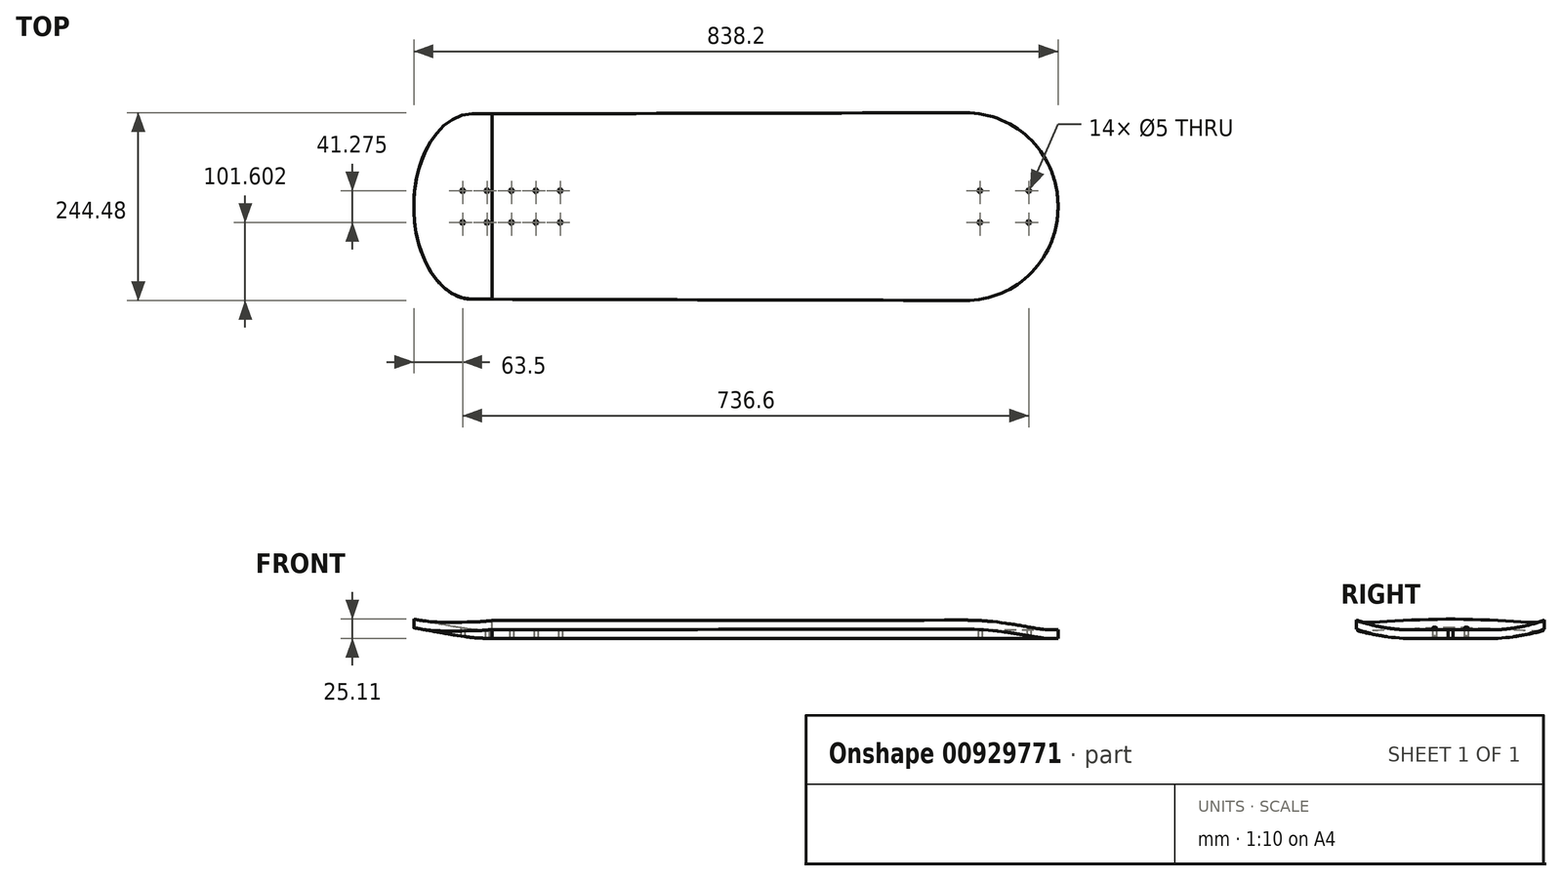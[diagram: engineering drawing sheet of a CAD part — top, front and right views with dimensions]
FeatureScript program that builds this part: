
annotation { "Feature Type Name" : "Feature", "Feature Type Description" : "" }
export const myFeature = defineFeature(function(context is Context, id is Id, definition is map)
    precondition{}
    {
        {
            var Q0;
            Q0=qCreatedBy(makeId("Front.planeOp"),FACE);
            var sketch = newSketch(context, id + "F0", { "sketchPlane" : qUnion([Q0])});
            skPoint(sketch, "E0", {"position": v(-774.7, 0) * mm});
            skPoint(sketch, "E1", {"position": v(-711.2, 0) * mm});
            skPoint(sketch, "E2", {"position": v(-742.95, 0) * mm});
            skPoint(sketch, "E3", {"position": v(-38.1, 0) * mm});
            skPoint(sketch, "E4", {"position": v(-647.7, 0) * mm});
            skPoint(sketch, "E5", {"position": v(-679.45, 0) * mm});
            skPoint(sketch, "E6", {"position": v(-101.6, 0) * mm});
            skLineSegment(sketch, "E7", {"start": v(0, 0) * mm, "end": v(-736.6, 0) * mm});
            skLineSegment(sketch, "E8", {"start": v(-780.7, 3.86) * mm, "end": v(-838.2, 14) * mm});
            skArc(sketch, "E9.filletArc", {"start": v(-780.7, 3.86) * mm, "mid": v(-758.74, 0.97) * mm, "end": v(-736.6, 0) * mm});
            skSolve(sketch);
        }
        {
            var Q0;
            Q0=qCreatedBy(makeId("Top.planeOp"),FACE);
            var sketch = newSketch(context, id + "F1", { "sketchPlane" : qUnion([Q0])});
            skLineSegment(sketch, "E10", {"start": v(-762.12, 120.65) * mm, "end": v(-120.94, 122.24) * mm});
            skLineSegment(sketch, "E11", {"start": v(-120.94, -122.24) * mm, "end": v(-762.12, -120.65) * mm});
            skArc(sketch, "E12.filletArc", {"start": v(0, 0) * mm, "mid": v(-34.87, 86.44) * mm, "end": v(-120.94, 122.24) * mm});
            skArc(sketch, "E13.filletArc", {"start": v(-120.94, -122.24) * mm, "mid": v(-34.87, -86.44) * mm, "end": v(0, 0) * mm});
            skPoint(sketch, "E14.visualSharp", {"position": v(-762.12, 120.65) * mm});
            skPoint(sketch, "E15.visualSharp", {"position": v(-762.12, -120.65) * mm});
            skPoint(sketch, "E16", {"position": v(-120.64, -122.24) * mm});
            skPoint(sketch, "E17", {"position": v(-120.64, 122.24) * mm});
            skPoint(sketch, "E18.5", {"position": v(-774.7, 0) * mm});
            skPoint(sketch, "E18.6", {"position": v(-711.2, 0) * mm});
            skPoint(sketch, "E18.7", {"position": v(-742.95, 0) * mm});
            skPoint(sketch, "E18.8", {"position": v(-38.1, 0) * mm});
            skPoint(sketch, "E18.9", {"position": v(-647.7, 0) * mm});
            skPoint(sketch, "E18.10", {"position": v(-679.45, 0) * mm});
            skPoint(sketch, "E18.11", {"position": v(-101.6, 0) * mm});
            skLineSegment(sketch, "E19", {"start": v(-774.7, 0) * mm, "end": v(-774.7, 20.64) * mm, "construction": true});
            skLineSegment(sketch, "E20", {"start": v(-711.2, 20.64) * mm, "end": v(-711.2, 0) * mm, "construction": true});
            skLineSegment(sketch, "E21", {"start": v(-38.1, 0) * mm, "end": v(-38.1, 20.64) * mm, "construction": true});
            skLineSegment(sketch, "E22", {"start": v(-647.7, 0) * mm, "end": v(-647.7, 20.64) * mm, "construction": true});
            skLineSegment(sketch, "E23", {"start": v(-101.6, 0) * mm, "end": v(-101.6, 20.64) * mm, "construction": true});
            skLineSegment(sketch, "E24", {"start": v(-679.45, 0) * mm, "end": v(-679.45, 20.64) * mm, "construction": true});
            skLineSegment(sketch, "E25", {"start": v(-742.95, 0) * mm, "end": v(-742.95, 20.64) * mm, "construction": true});
            skCircle(sketch, "E26", {"center": v(-774.7, 20.64) * mm, "radius": 2.5 * mm});
            skCircle(sketch, "E27", {"center": v(-711.2, 20.64) * mm, "radius": 2.5 * mm});
            skCircle(sketch, "E28", {"center": v(-742.95, 20.64) * mm, "radius": 2.5 * mm});
            skCircle(sketch, "E29", {"center": v(-679.45, 20.64) * mm, "radius": 2.5 * mm});
            skCircle(sketch, "E30", {"center": v(-101.6, 20.64) * mm, "radius": 2.5 * mm});
            skCircle(sketch, "E31", {"center": v(-647.7, 20.64) * mm, "radius": 2.5 * mm});
            skCircle(sketch, "E32", {"center": v(-38.1, 20.64) * mm, "radius": 2.5 * mm});
            skCircle(sketch, "E33.MirrorC", {"center": v(-38.1, -20.64) * mm, "radius": 2.5 * mm});
            skCircle(sketch, "E34.MirrorC", {"center": v(-647.7, -20.64) * mm, "radius": 2.5 * mm});
            skCircle(sketch, "E35.MirrorC", {"center": v(-101.6, -20.64) * mm, "radius": 2.5 * mm});
            skCircle(sketch, "E36.MirrorC", {"center": v(-679.45, -20.64) * mm, "radius": 2.5 * mm});
            skCircle(sketch, "E37.MirrorC", {"center": v(-742.95, -20.64) * mm, "radius": 2.5 * mm});
            skCircle(sketch, "E38.MirrorC", {"center": v(-711.2, -20.64) * mm, "radius": 2.5 * mm});
            skCircle(sketch, "E39.MirrorC", {"center": v(-774.7, -20.64) * mm, "radius": 2.5 * mm});
            skLineSegment(sketch, "E40", {"start": v(-647.7, 0) * mm, "end": v(-647.7, -20.64) * mm, "construction": true});
            skPoint(sketch, "E41", {"position": v(-838.2, 0) * mm});
            skEllipticalArc(sketch, "E42", {});
            skPoint(sketch, "E43", {"position": v(-762, -120.65) * mm});
            const initialGuessF1  = {"E42": [-0.762, 0, 0, 1, 0.12065014743999705, 0.0762, 0.001563359187813156, 3.141592653589793]};
            skSetInitialGuess(sketch, initialGuessF1);
            skSolve(sketch);
        }
        {
            var Q0;
            Q0=sQuery(id+"F0.wireOp",VERTEX,"E8.end");
            var Q1;
            Q1=sQuery(id+"F0.wireOp",EDGE,"E8");
            cPlane(context, id + "F2", {"entities" : qUnion([Q0, Q1]), "cplaneType" : CPlaneType.LINE_POINT, "offset" : 25.4 * mm, "width" : 152.4 * mm, "height" : 152.4 * mm});
        }
        {
            var Q0;
            Q0=sQuery(id+"F0.wireOp",VERTEX,"E7.end");
            var Q1;
            Q1=sQuery(id+"F0.wireOp",EDGE,"E7");
            cPlane(context, id + "F3", {"entities" : qUnion([Q0, Q1]), "cplaneType" : CPlaneType.LINE_POINT, "offset" : 25.4 * mm, "width" : 152.4 * mm, "height" : 152.4 * mm});
        }
        {
            var Q0;
            Q0=sQuery(id+"F0.wireOp",VERTEX,"E7.start");
            var Q1;
            Q1=sQuery(id+"F0.wireOp",EDGE,"E7");
            cPlane(context, id + "F4", {"entities" : qUnion([Q0, Q1]), "cplaneType" : CPlaneType.LINE_POINT, "offset" : 25.4 * mm, "width" : 152.4 * mm, "height" : 152.4 * mm});
        }
        {
            var Q0;
            Q0=qCreatedBy(id+"F4.planeOp",FACE);
            var sketch = newSketch(context, id + "F5", { "sketchPlane" : qUnion([Q0])});
            skLineSegment(sketch, "E44", {"start": v(0, -32.26) * mm, "end": v(0, 0) * mm, "construction": true});
            skLineSegment(sketch, "E45", {"start": v(0, 218.6) * mm, "end": v(0, 0) * mm, "construction": true});
            skLineSegment(sketch, "E46", {"start": v(0, 0) * mm, "end": v(-50.8, 0) * mm});
            skArc(sketch, "E47", {"start": v(-122.24, 12.7) * mm, "mid": v(-87.08, 3.2) * mm, "end": v(-50.8, 0) * mm});
            skArc(sketch, "E48", {"start": v(-122.24, 0.9) * mm, "mid": v(-87.02, -8.09) * mm, "end": v(-50.8, -11.11) * mm});
            skLineSegment(sketch, "E49", {"start": v(-122.24, 12.7) * mm, "end": v(-122.24, 0.9) * mm});
            skLineSegment(sketch, "E50", {"start": v(-50.8, -11.11) * mm, "end": v(0, -11.11) * mm});
            skLineSegment(sketch, "E51.MirrorCS", {"start": v(122.24, 12.7) * mm, "end": v(122.24, 0.9) * mm});
            skArc(sketch, "E52.MirrorCS", {"start": v(122.24, 0.9) * mm, "mid": v(87.02, -8.09) * mm, "end": v(50.8, -11.11) * mm});
            skLineSegment(sketch, "E53.MirrorCS", {"start": v(0, 0) * mm, "end": v(50.8, 0) * mm});
            skLineSegment(sketch, "E54.MirrorCS", {"start": v(50.8, -11.11) * mm, "end": v(0, -11.11) * mm});
            skArc(sketch, "E55.MirrorCS", {"start": v(122.24, 12.7) * mm, "mid": v(87.08, 3.2) * mm, "end": v(50.8, 0) * mm});
            skSolve(sketch);
        }
        {
            var Q0;
            Q0=qCreatedBy(id+"F3.planeOp",FACE);
            var sketch = newSketch(context, id + "F6", { "sketchPlane" : qUnion([Q0])});
            skLineSegment(sketch, "E56.0", {"start": v(0, -32.26) * mm, "end": v(0, 0) * mm, "construction": true});
            skLineSegment(sketch, "E56.1", {"start": v(0, 218.6) * mm, "end": v(0, 0) * mm, "construction": true});
            skLineSegment(sketch, "E56.2", {"start": v(0, 0) * mm, "end": v(-50.8, 0) * mm});
            skArc(sketch, "E56.3", {"start": v(-122.24, 12.7) * mm, "mid": v(-87.08, 3.2) * mm, "end": v(-50.8, 0) * mm});
            skArc(sketch, "E56.4", {"start": v(-122.24, 0.9) * mm, "mid": v(-87.02, -8.09) * mm, "end": v(-50.8, -11.11) * mm});
            skLineSegment(sketch, "E56.5", {"start": v(-122.24, 12.7) * mm, "end": v(-122.24, 0.9) * mm});
            skLineSegment(sketch, "E56.6", {"start": v(-50.8, -11.11) * mm, "end": v(0, -11.11) * mm});
            skLineSegment(sketch, "E56.7", {"start": v(122.24, 12.7) * mm, "end": v(122.24, 0.9) * mm});
            skArc(sketch, "E56.8", {"start": v(122.24, 0.9) * mm, "mid": v(87.02, -8.09) * mm, "end": v(50.8, -11.11) * mm});
            skLineSegment(sketch, "E56.9", {"start": v(0, 0) * mm, "end": v(50.8, 0) * mm});
            skLineSegment(sketch, "E56.10", {"start": v(50.8, -11.11) * mm, "end": v(0, -11.11) * mm});
            skArc(sketch, "E56.11", {"start": v(122.24, 12.7) * mm, "mid": v(87.08, 3.2) * mm, "end": v(50.8, 0) * mm});
            skSolve(sketch);
        }
        {
            var Q0;
            Q0=qCreatedBy(id+"F2.planeOp",FACE);
            var sketch = newSketch(context, id + "F7", { "sketchPlane" : qUnion([Q0])});
            skLineSegment(sketch, "E57", {"start": v(0, -131.77) * mm, "end": v(-50.8, -131.77) * mm});
            skLineSegment(sketch, "E58", {"start": v(-50.8, -131.77) * mm, "end": v(-122.24, -131.77) * mm});
            skLineSegment(sketch, "E59", {"start": v(-122.24, -131.77) * mm, "end": v(-122.24, -142.88) * mm});
            skLineSegment(sketch, "E60", {"start": v(-122.24, -142.88) * mm, "end": v(-50.8, -142.88) * mm});
            skLineSegment(sketch, "E61", {"start": v(-50.8, -142.88) * mm, "end": v(0, -142.88) * mm});
            skLineSegment(sketch, "E62", {"start": v(0, -142.88) * mm, "end": v(50.8, -142.88) * mm});
            skLineSegment(sketch, "E63", {"start": v(50.8, -142.88) * mm, "end": v(122.24, -142.88) * mm});
            skLineSegment(sketch, "E64", {"start": v(122.24, -142.88) * mm, "end": v(122.24, -131.77) * mm});
            skLineSegment(sketch, "E65", {"start": v(122.24, -131.77) * mm, "end": v(50.8, -131.77) * mm});
            skLineSegment(sketch, "E66", {"start": v(50.8, -131.77) * mm, "end": v(0, -131.77) * mm});
            skSolve(sketch);
        }
        {
            var Q0;
            Q0=qCreatedBy(makeId("Front.planeOp"),FACE);
            var Q1;
            Q1=sQuery(id+"F5.wireOp",VERTEX,"E47.start");
            cPlane(context, id + "F8", {"entities" : qUnion([Q0, Q1]), "cplaneType" : CPlaneType.PLANE_POINT, "offset" : 25.4 * mm, "width" : 152.4 * mm, "height" : 152.4 * mm});
        }
        {
            var Q0;
            Q0=qCreatedBy(makeId("Front.planeOp"),FACE);
            var Q1;
            Q1=sQuery(id+"F5.wireOp",VERTEX,"E51.MirrorCS.start");
            cPlane(context, id + "F9", {"entities" : qUnion([Q0, Q1]), "cplaneType" : CPlaneType.PLANE_POINT, "offset" : 25.4 * mm, "width" : 152.4 * mm, "height" : 152.4 * mm});
        }
        {
            var Q0;
            Q0=qCreatedBy(id+"F8.planeOp",FACE);
            var sketch = newSketch(context, id + "F10", { "sketchPlane" : qUnion([Q0])});
            skLineSegment(sketch, "E67", {"start": v(0, 12.7) * mm, "end": v(-736.6, 12.7) * mm});
            skLineSegment(sketch, "E68", {"start": v(-730.31, 12.66) * mm, "end": v(-838.2, 14) * mm});
            skPoint(sketch, "E69.visualSharp", {"position": v(-733.46, 12.7) * mm});
            skArc(sketch, "E69.filletArc", {"start": v(-736.6, 12.7) * mm, "mid": v(-739.74, -1003.3) * mm, "end": v(-730.31, 12.66) * mm});
            skSolve(sketch);
        }
        {
            var Q0;
            Q0 = qSketchRegion(id + "F5", true);
            var Q1;
            Q1=sQuery(id+"F6.wireOp",VERTEX,"E56.0.end");
            extrude(context, id + "F11", {"entities" : qUnion([Q0]), "endBound" : BoundingType.UP_TO_VERTEX, "depth" : 25.4 * mm, "endBoundEntityVertex" : qUnion([Q1]), "offsetDistance" : 25.4 * mm});
        }
        {
            var Q0;
            Q0 = qConstructionFilter(qBodyType(qCreatedBy(id + "F0" ,EDGE), BodyType.WIRE), ConstructionObject.NO);
            var Q2;
            Q2 = qSketchRegion(id + "F6", true);
            var Q3;
            Q3 = qSketchRegion(id + "F7", true);
            loft(context, id + "F12", {"operationType" : NewBodyOperationType.ADD, "addSections" : true, "spine" : qUnion([Q0]), "sectionCount" : 5, "sheetProfilesArray" : [{ "sheetProfileEntities" : qUnion([Q2]) }, { "sheetProfileEntities" : qUnion([Q3]) }]});
        }
        {
            var Q0;
            Q0 = qSketchRegion(id + "F1", true);
            extrude(context, id + "F13", {"entities" : qUnion([Q0]), "endBound" : BoundingType.THROUGH_ALL, "depth" : 25.4 * mm, "offsetDistance" : 25.4 * mm, "hasSecondDirection" : true, "secondDirectionBound" : SecondDirectionBoundingType.THROUGH_ALL, "secondDirectionOppositeDirection" : true, "secondDirectionDepth" : 25.4 * mm});
        }
        {
            var Q0;
            Q0=makeQuery(id+"F11.opExtrude","SWEPT_BODY",BODY,{"disambiguationData":[OSD([sQuery(id+"F5.wireOp",EDGE,"E46"),sQuery(id+"F5.wireOp",EDGE,"E47"),sQuery(id+"F5.wireOp",EDGE,"E48"),sQuery(id+"F5.wireOp",EDGE,"E49"),sQuery(id+"F5.wireOp",EDGE,"E50"),sQuery(id+"F5.wireOp",EDGE,"E51.MirrorCS"),sQuery(id+"F5.wireOp",EDGE,"E52.MirrorCS"),sQuery(id+"F5.wireOp",EDGE,"E53.MirrorCS"),sQuery(id+"F5.wireOp",EDGE,"E54.MirrorCS"),sQuery(id+"F5.wireOp",EDGE,"E55.MirrorCS")])]});
            var Q1;
            Q1=makeQuery(id+"F13.opExtrude","SWEPT_BODY",BODY,{"disambiguationData":[OSD([sQuery(id+"F1.wireOp",EDGE,"E10"),sQuery(id+"F1.wireOp",EDGE,"E11"),sQuery(id+"F1.wireOp",EDGE,"E12.filletArc"),sQuery(id+"F1.wireOp",EDGE,"E13.filletArc"),sQuery(id+"F1.wireOp",EDGE,"OMjmO50u-64Dg-kMjp-lwE1-YGDWL1Mbj6oi"),sQuery(id+"F1.wireOp",EDGE,"E14.filletArc"),sQuery(id+"F1.wireOp",EDGE,"E15.filletArc"),sQuery(id+"F1.wireOp",EDGE,"E26"),sQuery(id+"F1.wireOp",EDGE,"E27"),sQuery(id+"F1.wireOp",EDGE,"E28"),sQuery(id+"F1.wireOp",EDGE,"E29"),sQuery(id+"F1.wireOp",EDGE,"E30"),sQuery(id+"F1.wireOp",EDGE,"E31"),sQuery(id+"F1.wireOp",EDGE,"E32"),sQuery(id+"F1.wireOp",EDGE,"E33.MirrorC"),sQuery(id+"F1.wireOp",EDGE,"E34.MirrorC"),sQuery(id+"F1.wireOp",EDGE,"E35.MirrorC"),sQuery(id+"F1.wireOp",EDGE,"E36.MirrorC"),sQuery(id+"F1.wireOp",EDGE,"E37.MirrorC"),sQuery(id+"F1.wireOp",EDGE,"E38.MirrorC"),sQuery(id+"F1.wireOp",EDGE,"E39.MirrorC")])]});
            booleanBodies(context, id + "F14", {"operationType" : BooleanOperationType.INTERSECTION, "tools" : qUnion([Q0, Q1])});
        }
    });
